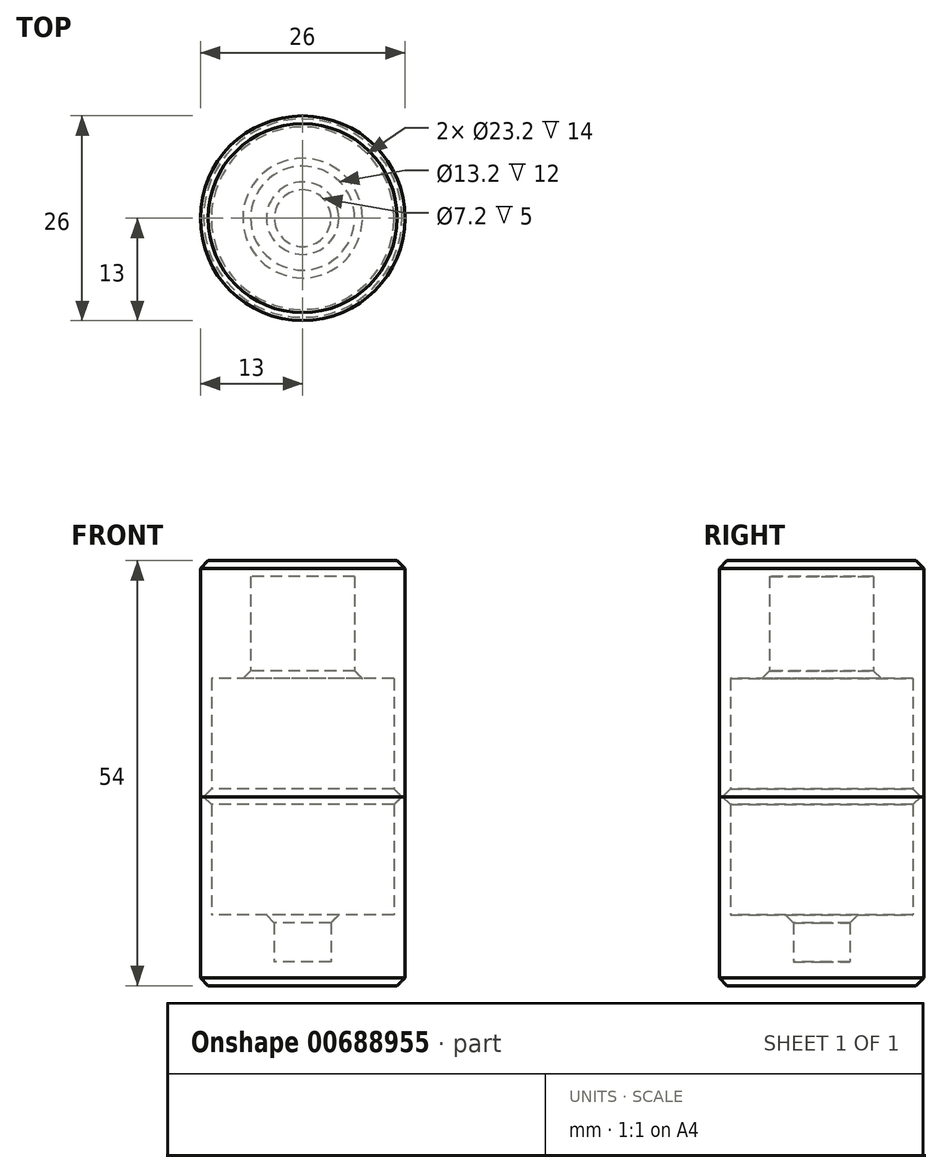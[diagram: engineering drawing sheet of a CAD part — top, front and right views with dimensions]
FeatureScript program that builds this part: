
annotation { "Feature Type Name" : "Feature", "Feature Type Description" : "" }
export const myFeature = defineFeature(function(context is Context, id is Id, definition is map)
    precondition{}
    {
        {
            var Q0;
            Q0=qCreatedBy(makeId("Top.planeOp"),FACE);
            var sketch = newSketch(context, id + "F0", { "sketchPlane" : qUnion([Q0])});
            skCircle(sketch, "E0", {"center": v(0, 0) * mm, "radius": 13 * mm});
            skCircle(sketch, "E1", {"center": v(0, 0) * mm, "radius": 3.6 * mm});
            skSolve(sketch);
        }
        {
            var Q0;
            Q0=makeQuery(id+"F0.imprint","IMPRINT",FACE,{"disambiguationData":[TD([[makeQuery(id+"F0.imprint","IMPRINT",EDGE,{"derivedFrom":sQuery(id+"F0.wireOp",EDGE,"E1")}),1.0]])]});
            extrude(context, id + "F1", {"entities" : qUnion([Q0]), "depth" : 3 * mm, "offsetDistance" : 25 * mm});
        }
        {
            var Q0;
            Q0 = qSketchRegion(id + "F0", true);
            extrude(context, id + "F2", {"entities" : qUnion([Q0]), "operationType" : NewBodyOperationType.ADD, "depth" : (3 + 6) * mm, "offsetDistance" : 25 * mm});
        }
        {
            var Q0;
            Q0=makeQuery(id+"F2.opExtrude","CAP_FACE",FACE,{"disambiguationData":[OSD([sQuery(id+"F0.wireOp",EDGE,"E0"),sQuery(id+"F0.wireOp",EDGE,"E1")])],"isStart":false});
            var sketch = newSketch(context, id + "F3", { "sketchPlane" : qUnion([Q0])});
            skCircle(sketch, "E2", {"center": v(0, 0) * mm, "radius": 11.6 * mm});
            skSolve(sketch);
        }
        {
            var Q0;
            Q0=makeQuery(id+"F3.imprint","IMPRINT",FACE,{"disambiguationData":[TD([[makeQuery(id+"F3.imprint","IMPRINT",EDGE,{"derivedFrom":sQuery(id+"F3.wireOp",EDGE,"E2")}),-1.0]])]});
            extrude(context, id + "F4", {"entities" : qUnion([Q0]), "operationType" : NewBodyOperationType.ADD, "depth" : 15 * mm, "offsetDistance" : 25 * mm});
        }
        {
            var Q0;
            Q0=makeQuery(id+"F4.opExtrude","CAP_FACE",FACE,{"disambiguationData":[OSD([sQuery(id+"F0.wireOp",EDGE,"E0"),sQuery(id+"F3.wireOp",EDGE,"E2")])],"isStart":false});
            var sketch = newSketch(context, id + "F5", { "sketchPlane" : qUnion([Q0])});
            skSolve(sketch);
        }
        {
            var Q0;
            Q0 = qSketchRegion(id + "F5", true);
            var Q1;
            Q1=makeQuery(id+"F5.imprint","IMPRINT",FACE,{"disambiguationData":[TD([[makeQuery(id+"F5.imprint","IMPRINT",EDGE,{"derivedFrom":makeQuery(id+"F4.opExtrude","CAP_EDGE",EDGE,{"disambiguationData":[OSD([sQuery(id+"F3.wireOp",EDGE,"E2")])],"isStart":false})}),-1.0]])]});
            extrude(context, id + "F6", {"entities" : qUnion([Q0, Q1]), "depth" : 15 * mm, "offsetDistance" : 25 * mm});
        }
        {
            var Q0;
            Q0=makeQuery(id+"F6.opExtrude","CAP_FACE",FACE,{"disambiguationData":[OSD([sQuery(id+"F0.wireOp",EDGE,"E0"),sQuery(id+"F3.wireOp",EDGE,"E2")])],"isStart":false});
            var sketch = newSketch(context, id + "F7", { "sketchPlane" : qUnion([Q0])});
            skCircle(sketch, "E3.0", {"center": v(0, 0) * mm, "radius": 11.6 * mm});
            skCircle(sketch, "E4.0", {"center": v(0, 0) * mm, "radius": 13 * mm});
            skCircle(sketch, "E5", {"center": v(0, 0) * mm, "radius": 6.6 * mm});
            skSolve(sketch);
        }
        {
            var Q0;
            Q0 = qSketchRegion(id + "F7", true);
            var Q1;
            Q1=makeQuery(id+"F7.imprint","IMPRINT",FACE,{"disambiguationData":[TD([[makeQuery(id+"F7.imprint","IMPRINT",EDGE,{"derivedFrom":sQuery(id+"F7.wireOp",EDGE,"E3.0")}),1.0]])]});
            extrude(context, id + "F8", {"entities" : qUnion([Q0, Q1]), "operationType" : NewBodyOperationType.ADD, "depth" : 13 * mm, "offsetDistance" : 25 * mm});
        }
        {
            var Q0;
            Q0=makeQuery(id+"F8.opExtrude","CAP_FACE",FACE,{"disambiguationData":[OSD([sQuery(id+"F7.wireOp",EDGE,"E4.0"),sQuery(id+"F7.wireOp",EDGE,"E5")])],"isStart":false});
            var sketch = newSketch(context, id + "F9", { "sketchPlane" : qUnion([Q0])});
            skCircle(sketch, "E6.0", {"center": v(0, 0) * mm, "radius": 13 * mm});
            skSolve(sketch);
        }
        {
            var Q0;
            Q0=makeQuery(id+"F9.imprint","IMPRINT",FACE,{"disambiguationData":[TD([[makeQuery(id+"F9.imprint","IMPRINT",EDGE,{"derivedFrom":sQuery(id+"F9.wireOp",EDGE,"E6.0")}),1.0]])]});
            var Q1;
            Q1=makeQuery(id+"F9.imprint","IMPRINT",FACE,{"disambiguationData":[TD([[makeQuery(id+"F9.imprint","IMPRINT",EDGE,{"derivedFrom":makeQuery(id+"F8.opExtrude","CAP_EDGE",EDGE,{"disambiguationData":[OSD([sQuery(id+"F7.wireOp",EDGE,"E5")])],"isStart":false})}),1.0]])]});
            extrude(context, id + "F10", {"entities" : qUnion([Q0, Q1]), "operationType" : NewBodyOperationType.ADD, "depth" : 2 * mm, "offsetDistance" : 25 * mm});
        }
        {
            var Q0;
            Q0=makeQuery(id+"F4.opExtrude","CAP_EDGE",EDGE,{"disambiguationData":[OSD([sQuery(id+"F3.wireOp",EDGE,"E2")])],"isStart":false});
            var Q1;
            Q1=makeQuery(id+"F2.opExtrude","CAP_EDGE",EDGE,{"disambiguationData":[OSD([sQuery(id+"F0.wireOp",EDGE,"E1")])],"isStart":false});
            var Q2;
            Q2=makeQuery(id+"F2.opExtrude","CAP_EDGE",EDGE,{"disambiguationData":[OSD([sQuery(id+"F0.wireOp",EDGE,"E0")])],"isStart":true});
            chamfer(context, id + "F11", {"entities" : qUnion([Q0, Q1, Q2]), "width" : 1 * mm, "tangentPropagation" : true});
        }
        {
            var Q0;
            Q0=makeQuery(id+"F8.opExtrude","CAP_EDGE",EDGE,{"disambiguationData":[OSD([sQuery(id+"F7.wireOp",EDGE,"E5")])],"isStart":true});
            var Q1;
            Q1=makeQuery(id+"F6.opExtrude","CAP_EDGE",EDGE,{"disambiguationData":[OSD([sQuery(id+"F3.wireOp",EDGE,"E2")])],"isStart":true});
            var Q2;
            Q2=makeQuery(id+"F10.opExtrude","CAP_EDGE",EDGE,{"disambiguationData":[OSD([sQuery(id+"F9.wireOp",EDGE,"E6.0")])],"isStart":false});
            chamfer(context, id + "F12", {"entities" : qUnion([Q0, Q1, Q2]), "width" : 1 * mm, "tangentPropagation" : true});
        }
    });
